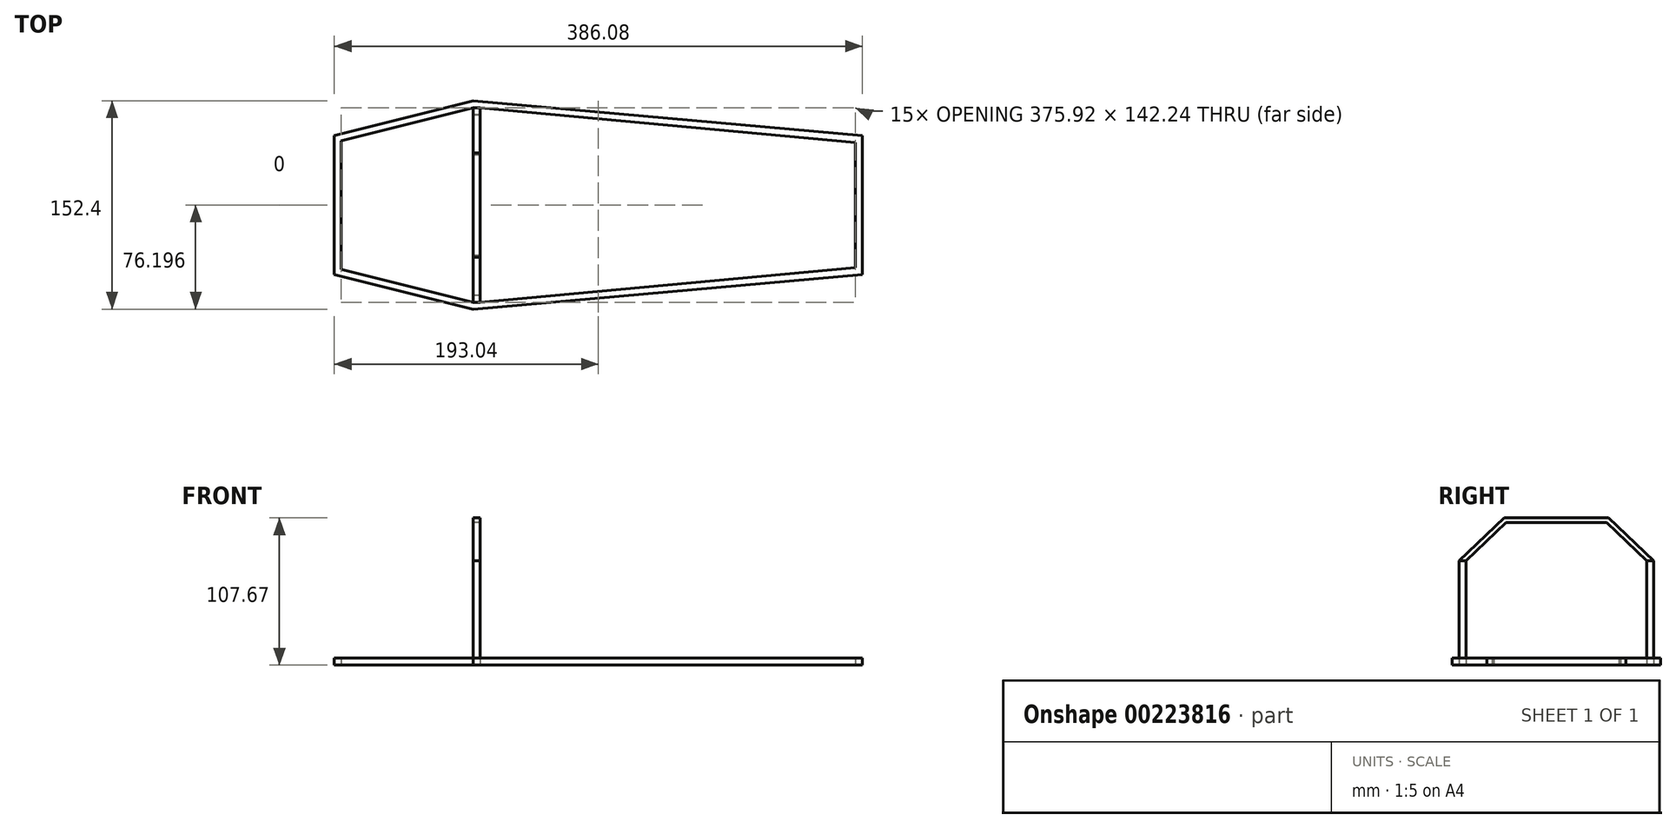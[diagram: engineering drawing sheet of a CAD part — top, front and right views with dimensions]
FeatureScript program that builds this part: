
annotation { "Feature Type Name" : "Feature", "Feature Type Description" : "" }
export const myFeature = defineFeature(function(context is Context, id is Id, definition is map)
    precondition{}
    {
        {
            var Q0;
            Q0=qCreatedBy(makeId("Top.planeOp"),FACE);
            var sketch = newSketch(context, id + "F0", { "sketchPlane" : qUnion([Q0])});
            skLineSegment(sketch, "E0", {"start": v(-101.67, 50.9) * mm, "end": v(-101.67, -50.7) * mm});
            skLineSegment(sketch, "E1", {"start": v(284.4, 50.9) * mm, "end": v(284.4, -50.7) * mm});
            skLineSegment(sketch, "E2", {"start": v(-0.07, 76.3) * mm, "end": v(-0.07, -76.1) * mm});
            skPoint(sketch, "E3", {"position": v(-0.07, 0.1) * mm});
            skLineSegment(sketch, "E4", {"start": v(-101.67, 50.9) * mm, "end": v(-0.07, 76.3) * mm});
            skLineSegment(sketch, "E5", {"start": v(-101.67, -50.7) * mm, "end": v(-0.07, -76.1) * mm});
            skLineSegment(sketch, "E6", {"start": v(-0.07, 76.3) * mm, "end": v(5, 71.22) * mm});
            skLineSegment(sketch, "E7", {"start": v(5, 71.22) * mm, "end": v(5, -71.02) * mm});
            skLineSegment(sketch, "E8", {"start": v(-0.07, -76.1) * mm, "end": v(5, -71.02) * mm});
            skLineSegment(sketch, "E9", {"start": v(279.33, 45.82) * mm, "end": v(279.33, -45.62) * mm});
            skLineSegment(sketch, "E10", {"start": v(279.33, 45.82) * mm, "end": v(284.4, 50.9) * mm});
            skLineSegment(sketch, "E11", {"start": v(279.33, -45.62) * mm, "end": v(284.4, -50.7) * mm});
            skLineSegment(sketch, "E12", {"start": v(-0.07, -76.1) * mm, "end": v(284.4, -50.7) * mm});
            skLineSegment(sketch, "E13", {"start": v(279.33, -45.62) * mm, "end": v(5, -71.02) * mm});
            skLineSegment(sketch, "E14", {"start": v(-0.07, 76.3) * mm, "end": v(284.4, 50.9) * mm});
            skLineSegment(sketch, "E15", {"start": v(279.33, 45.82) * mm, "end": v(5, 71.22) * mm});
            skPoint(sketch, "E16", {"position": v(-0.07, 71.22) * mm});
            skPoint(sketch, "E17", {"position": v(-0.07, -71.02) * mm});
            skLineSegment(sketch, "E18", {"start": v(-96.6, 46.9) * mm, "end": v(-0.07, 71.22) * mm});
            skLineSegment(sketch, "E19", {"start": v(-101.67, 50.9) * mm, "end": v(-96.6, 46.9) * mm});
            skLineSegment(sketch, "E20", {"start": v(-0.07, -71.02) * mm, "end": v(-96.6, -46.9) * mm});
            skLineSegment(sketch, "E21", {"start": v(-96.6, 46.9) * mm, "end": v(-96.6, -46.9) * mm});
            skLineSegment(sketch, "E22", {"start": v(-101.67, -50.7) * mm, "end": v(-96.6, -46.9) * mm});
            skLineSegment(sketch, "E23", {"start": v(-0.07, 71.22) * mm, "end": v(5, 71.22) * mm});
            skLineSegment(sketch, "E24", {"start": v(-0.07, 71.22) * mm, "end": v(-0.07, 66.15) * mm});
            skLineSegment(sketch, "E25", {"start": v(-0.07, 66.15) * mm, "end": v(5, 66.15) * mm});
            skLineSegment(sketch, "E26", {"start": v(5, 66.15) * mm, "end": v(5, 71.22) * mm});
            skLineSegment(sketch, "E27", {"start": v(-0.07, -71.02) * mm, "end": v(5, -71.02) * mm});
            skLineSegment(sketch, "E28", {"start": v(5, -71.02) * mm, "end": v(5, -65.93) * mm});
            skLineSegment(sketch, "E29", {"start": v(5, -65.93) * mm, "end": v(-0.07, -65.93) * mm});
            skLineSegment(sketch, "E30", {"start": v(-0.07, -65.93) * mm, "end": v(-0.07, -71.02) * mm});
            skSolve(sketch);
        }
        {
            var Q0;
            Q0 = qSketchRegion(id + "F0", true);
            extrude(context, id + "F1", {"entities" : qUnion([Q0]), "depth" : 5.08 * mm});
        }
        {
            var Q0;
            Q0=makeQuery(id+"F0.imprint","IMPRINT",FACE,{"disambiguationData":[TD([[makeQuery(id+"F0.imprint","IMPRINT",EDGE,{"derivedFrom":sQuery(id+"F0.wireOp",EDGE,"E7")}),-1.0]])]});
            extrude(context, id + "F2", {"entities" : qUnion([Q0]), "depth" : 5.08 * mm});
        }
        {
            var Q0;
            Q0=makeQuery(id+"F0.imprint","IMPRINT",FACE,{"disambiguationData":[TD([[makeQuery(id+"F0.imprint","IMPRINT",EDGE,{"derivedFrom":sQuery(id+"F0.wireOp",EDGE,"E27")}),1.0]])]});
            var Q1;
            Q1=makeQuery(id+"F0.imprint","IMPRINT",FACE,{"disambiguationData":[TD([[makeQuery(id+"F0.imprint","IMPRINT",EDGE,{"derivedFrom":sQuery(id+"F0.wireOp",EDGE,"E23")}),-1.0]])]});
            extrude(context, id + "F3", {"entities" : qUnion([Q0, Q1]), "depth" : 76.2 * mm});
        }
        {
            var Q0;
            Q0=qCreatedBy(makeId("Right.planeOp"),FACE);
            var sketch = newSketch(context, id + "F4", { "sketchPlane" : qUnion([Q0])});
            skLineSegment(sketch, "E31", {"start": v(0, 107.67) * mm, "end": v(38.1, 107.67) * mm});
            skLineSegment(sketch, "E32", {"start": v(0, 107.67) * mm, "end": v(-38.1, 107.67) * mm});
            skLineSegment(sketch, "E33", {"start": v(-71.02, 76.2) * mm, "end": v(-38.1, 107.67) * mm});
            skLineSegment(sketch, "E34", {"start": v(38.1, 107.67) * mm, "end": v(71.02, 76.2) * mm});
            skLineSegment(sketch, "E35", {"start": v(-65.94, 76.2) * mm, "end": v(-36.7, 104.16) * mm});
            skLineSegment(sketch, "E36", {"start": v(65.94, 76.2) * mm, "end": v(36.7, 104.16) * mm});
            skLineSegment(sketch, "E37", {"start": v(-36.7, 104.16) * mm, "end": v(36.7, 104.16) * mm});
            skLineSegment(sketch, "E38", {"start": v(36.7, 104.16) * mm, "end": v(38.1, 107.67) * mm});
            skLineSegment(sketch, "E39", {"start": v(-38.1, 107.67) * mm, "end": v(-36.7, 104.16) * mm});
            skLineSegment(sketch, "E40", {"start": v(-71.02, 76.2) * mm, "end": v(-65.94, 76.2) * mm});
            skLineSegment(sketch, "E41", {"start": v(65.94, 76.2) * mm, "end": v(71.02, 76.2) * mm});
            skLineSegment(sketch, "E42", {"start": v(-38.1, 107.67) * mm, "end": v(38.1, 107.67) * mm});
            skSolve(sketch);
        }
        {
            var Q0;
            Q0 = qSketchRegion(id + "F4", true);
            extrude(context, id + "F5", {"entities" : qUnion([Q0]), "depth" : 5.08 * mm});
        }
    });
